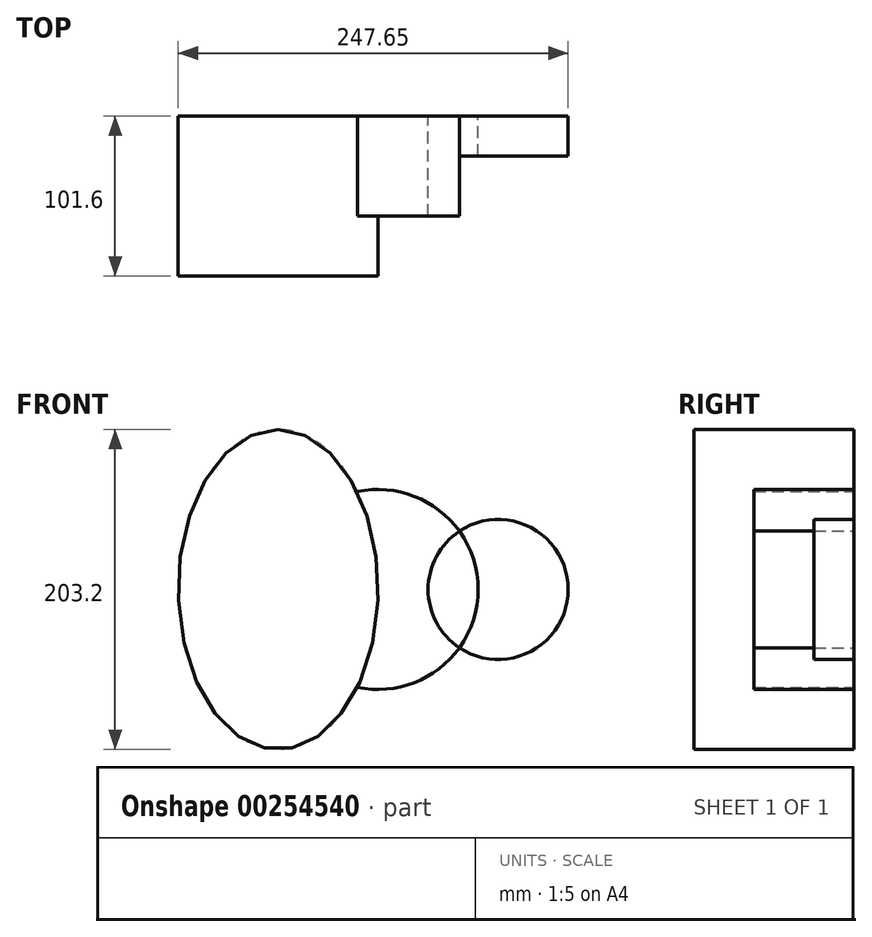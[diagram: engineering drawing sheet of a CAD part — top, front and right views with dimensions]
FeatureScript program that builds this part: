
annotation { "Feature Type Name" : "Feature", "Feature Type Description" : "" }
export const myFeature = defineFeature(function(context is Context, id is Id, definition is map)
    precondition{}
    {
        {
            var Q0;
            Q0=qCreatedBy(makeId("Front.planeOp"),FACE);
            var sketch = newSketch(context, id + "F0", { "sketchPlane" : qUnion([Q0])});
            skLineSegment(sketch, "E0", {"start": v(0, 0) * mm, "end": v(76.2, 0) * mm});
            skCircle(sketch, "E1", {"center": v(76.2, 0) * mm, "radius": 44.45 * mm});
            skLineSegment(sketch, "E2", {"start": v(31.75, 0) * mm, "end": v(63.5, 0) * mm});
            skCircle(sketch, "E3", {"center": v(0, 0) * mm, "radius": 63.5 * mm});
            skLineSegment(sketch, "E4", {"start": v(-63.5, 0) * mm, "end": v(-63.5, 101.6) * mm});
            skEllipse(sketch, "E5", {"center": v(-63.5, 0) * mm, "majorRadius": 101.6 * mm, "minorRadius": 63.5 * mm, "majorAxis": v(0, 1)});
            skSolve(sketch);
        }
        {
            var Q0;
            {var subQ0=sQuery(id+"F0.wireOp",EDGE,"E3");var subQ1=sQuery(id+"F0.wireOp",EDGE,"E1");var subQ2=makeQuery(id+"F0.imprint","INTERSECT",VERTEX,{"disambiguationData":[OD(0.0)],"derivedFrom":[subQ1,subQ0]});Q0=makeQuery(id+"F0.imprint","IMPRINT",FACE,{"disambiguationData":[TD([[makeQuery(id+"F0.imprint","IMPRINT",EDGE,{"disambiguationData":[TD([[subQ2,1.0]])],"derivedFrom":subQ1}),1.0]])]});}
            extrude(context, id + "F1", {"entities" : qUnion([Q0]), "depth" : 25.4 * mm});
        }
        {
            var Q0;
            {var subQ3=sQuery(id+"F0.wireOp",EDGE,"E1");var subQ5=sQuery(id+"F0.wireOp",EDGE,"E3");var subQ6=makeQuery(id+"F0.imprint","INTERSECT",VERTEX,{"disambiguationData":[OD(1.0)],"derivedFrom":[subQ3,subQ5]});Q0=makeQuery(id+"F0.imprint","IMPRINT",FACE,{"disambiguationData":[TD([[makeQuery(id+"F0.imprint","IMPRINT",EDGE,{"disambiguationData":[TD([[subQ6,1.0]])],"derivedFrom":subQ5}),1.0]])]});}
            var Q1;
            {var subQ0=sQuery(id+"F0.wireOp",EDGE,"E2");Q1=makeQuery(id+"F0.imprint","IMPRINT",FACE,{"disambiguationData":[TD([[makeQuery(id+"F0.imprint","IMPRINT",EDGE,{"derivedFrom":subQ0}),-1.0]])]});}
            var Q2;
            {var subQ3=sQuery(id+"F0.wireOp",EDGE,"E1");var subQ5=sQuery(id+"F0.wireOp",EDGE,"E3");var subQ6=makeQuery(id+"F0.imprint","INTERSECT",VERTEX,{"disambiguationData":[OD(0.0)],"derivedFrom":[subQ3,subQ5]});Q2=makeQuery(id+"F0.imprint","IMPRINT",FACE,{"disambiguationData":[TD([[makeQuery(id+"F0.imprint","IMPRINT",EDGE,{"disambiguationData":[TD([[subQ6,-1.0]])],"derivedFrom":subQ5}),1.0]])]});}
            var Q3;
            {var subQ0=sQuery(id+"F0.wireOp",EDGE,"E2");Q3=makeQuery(id+"F0.imprint","IMPRINT",FACE,{"disambiguationData":[TD([[makeQuery(id+"F0.imprint","IMPRINT",EDGE,{"derivedFrom":subQ0}),1.0]])]});}
            extrude(context, id + "F2", {"entities" : qUnion([Q0, Q1, Q2, Q3]), "operationType" : NewBodyOperationType.ADD, "depth" : 63.5 * mm});
        }
        {
            var Q0;
            {var subQ0=sQuery(id+"F0.wireOp",EDGE,"E4");Q0=makeQuery(id+"F0.imprint","IMPRINT",FACE,{"disambiguationData":[TD([[makeQuery(id+"F0.imprint","IMPRINT",EDGE,{"derivedFrom":subQ0}),1.0]])]});}
            var Q1;
            {var subQ0=sQuery(id+"F0.wireOp",EDGE,"E3");var subQ1=makeQuery(id+"F0.imprint","INTERSECT",VERTEX,{"derivedFrom":[subQ0,sQuery(id+"F0.wireOp",EDGE,"E4")]});Q1=makeQuery(id+"F0.imprint","IMPRINT",FACE,{"disambiguationData":[TD([[makeQuery(id+"F0.imprint","IMPRINT",EDGE,{"disambiguationData":[TD([[subQ1,1.0]])],"derivedFrom":subQ0}),1.0]])]});}
            var Q2;
            {var subQ0=sQuery(id+"F0.wireOp",EDGE,"E4");Q2=makeQuery(id+"F0.imprint","IMPRINT",FACE,{"disambiguationData":[TD([[makeQuery(id+"F0.imprint","IMPRINT",EDGE,{"derivedFrom":subQ0}),-1.0]])]});}
            extrude(context, id + "F3", {"entities" : qUnion([Q0, Q1, Q2]), "operationType" : NewBodyOperationType.ADD, "depth" : 101.6 * mm});
        }
    });
